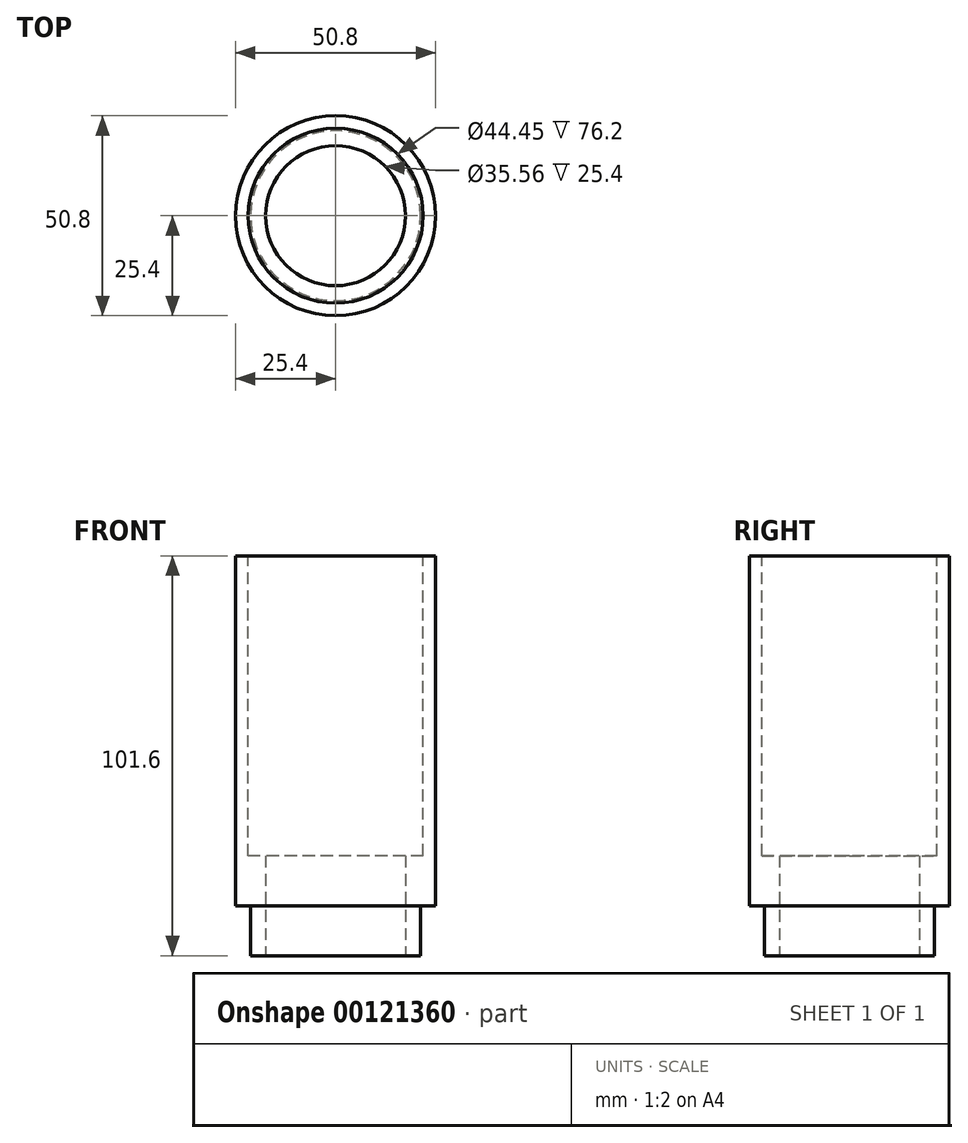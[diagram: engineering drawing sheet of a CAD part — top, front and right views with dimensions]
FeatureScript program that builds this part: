
annotation { "Feature Type Name" : "Feature", "Feature Type Description" : "" }
export const myFeature = defineFeature(function(context is Context, id is Id, definition is map)
    precondition{}
    {
        {
            var Q0;
            Q0=qCreatedBy(makeId("Top.planeOp"),FACE);
            var sketch = newSketch(context, id + "F0", { "sketchPlane" : qUnion([Q0])});
            skCircle(sketch, "E0", {"center": v(0, 0) * mm, "radius": 25.4 * mm});
            skSolve(sketch);
        }
        {
            var Q0;
            Q0 = qSketchRegion(id + "F0", true);
            extrude(context, id + "F1", {"entities" : qUnion([Q0]), "depth" : 88.9 * mm});
        }
        {
            var Q0;
            Q0=makeQuery(id+"F1.opExtrude","CAP_FACE",FACE,{"disambiguationData":[OSD([sQuery(id+"F0.wireOp",EDGE,"E0")])],"isStart":false});
            var sketch = newSketch(context, id + "F2", { "sketchPlane" : qUnion([Q0])});
            skCircle(sketch, "E1", {"center": v(0, 0) * mm, "radius": 22.23 * mm});
            skSolve(sketch);
        }
        {
            var Q0;
            Q0 = qSketchRegion(id + "F2", true);
            extrude(context, id + "F3", {"entities" : qUnion([Q0]), "operationType" : NewBodyOperationType.REMOVE, "oppositeDirection" : true, "depth" : 76.2 * mm});
        }
        {
            var Q0;
            Q0=makeQuery(id+"F1.opExtrude","CAP_FACE",FACE,{"disambiguationData":[OSD([sQuery(id+"F0.wireOp",EDGE,"E0")])],"isStart":true});
            var sketch = newSketch(context, id + "F4", { "sketchPlane" : qUnion([Q0])});
            skCircle(sketch, "E2", {"center": v(0, 0) * mm, "radius": 21.59 * mm});
            skSolve(sketch);
        }
        {
            var Q0;
            Q0 = qSketchRegion(id + "F4", true);
            extrude(context, id + "F5", {"entities" : qUnion([Q0]), "operationType" : NewBodyOperationType.ADD, "depth" : 12.7 * mm});
        }
        {
            var Q0;
            Q0=makeQuery(id+"F5.opExtrude","CAP_FACE",FACE,{"disambiguationData":[OSD([sQuery(id+"F4.wireOp",EDGE,"E2")])],"isStart":false});
            var sketch = newSketch(context, id + "F6", { "sketchPlane" : qUnion([Q0])});
            skCircle(sketch, "E3", {"center": v(0, 0) * mm, "radius": 17.78 * mm});
            skSolve(sketch);
        }
        {
            var Q0;
            Q0 = qSketchRegion(id + "F6", true);
            extrude(context, id + "F7", {"entities" : qUnion([Q0]), "operationType" : NewBodyOperationType.REMOVE, "endBound" : BoundingType.THROUGH_ALL, "oppositeDirection" : true, "depth" : 25.4 * mm});
        }
    });
